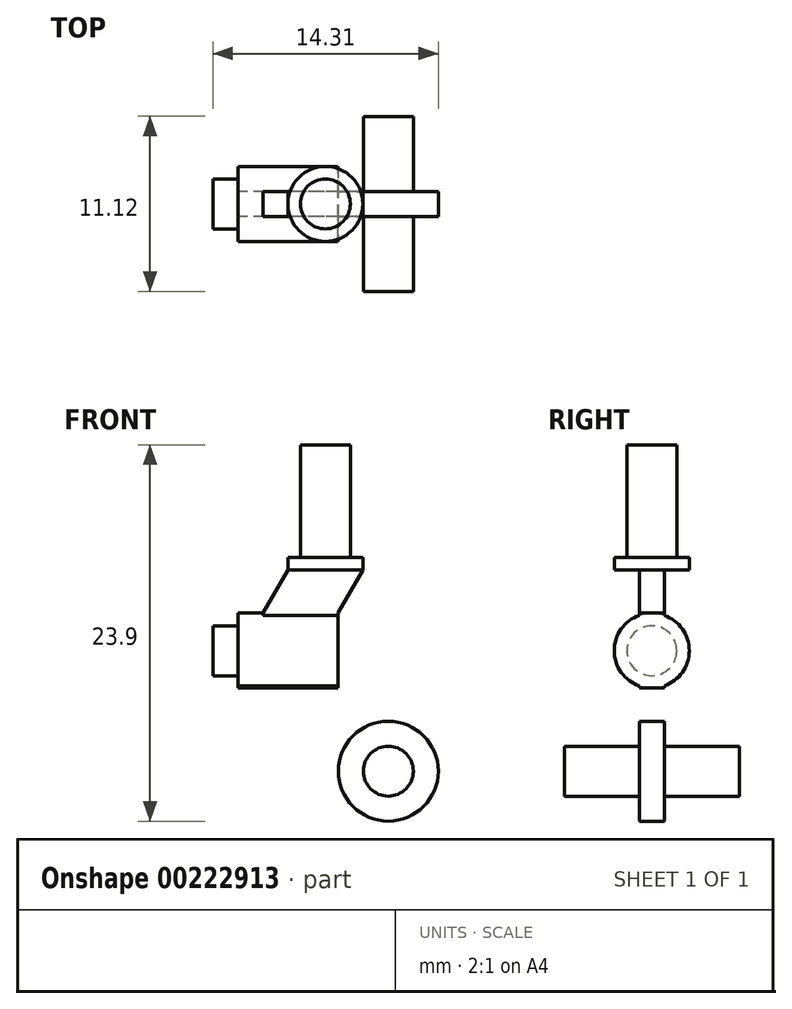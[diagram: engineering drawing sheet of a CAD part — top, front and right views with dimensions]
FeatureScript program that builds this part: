
annotation { "Feature Type Name" : "Feature", "Feature Type Description" : "" }
export const myFeature = defineFeature(function(context is Context, id is Id, definition is map)
    precondition{}
    {
        {
            var Q0;
            Q0=qCreatedBy(makeId("Top.planeOp"),FACE);
            var sketch = newSketch(context, id + "F0", { "sketchPlane" : qUnion([Q0])});
            skCircle(sketch, "E0", {"center": v(0, 0) * mm, "radius": 2.38 * mm});
            skCircle(sketch, "E1", {"center": v(0, 0) * mm, "radius": 1.59 * mm});
            skSolve(sketch);
        }
        {
            var Q0;
            Q0=makeQuery(id+"F0.imprint","IMPRINT",FACE,{"disambiguationData":[TD([[makeQuery(id+"F0.imprint","IMPRINT",EDGE,{"derivedFrom":sQuery(id+"F0.wireOp",EDGE,"E0")}),1.0]])]});
            extrude(context, id + "F1", {"entities" : qUnion([Q0]), "depth" : 0.8 * mm});
        }
        {
            var Q0;
            Q0=makeQuery(id+"F0.imprint","IMPRINT",FACE,{"disambiguationData":[TD([[makeQuery(id+"F0.imprint","IMPRINT",EDGE,{"derivedFrom":sQuery(id+"F0.wireOp",EDGE,"E1")}),1.0]])]});
            extrude(context, id + "F2", {"entities" : qUnion([Q0]), "operationType" : NewBodyOperationType.ADD, "depth" : 7.94 * mm});
        }
        {
            var Q0;
            Q0=qCreatedBy(makeId("Front.planeOp"),FACE);
            var sketch = newSketch(context, id + "F3", { "sketchPlane" : qUnion([Q0])});
            skLineSegment(sketch, "E2", {"start": v(0, 0) * mm, "end": v(-2.38, 0) * mm});
            skLineSegment(sketch, "E3", {"start": v(0, 0) * mm, "end": v(2.38, 0) * mm});
            skLineSegment(sketch, "E4", {"start": v(2.38, 0) * mm, "end": v(0.8, -2.75) * mm});
            skLineSegment(sketch, "E5", {"start": v(-2.38, 0) * mm, "end": v(-3.97, -2.75) * mm});
            skLineSegment(sketch, "E6", {"start": v(-3.97, -2.75) * mm, "end": v(0.8, -2.75) * mm});
            skLineSegment(sketch, "E7.bottom", {"start": v(0.8, -2.75) * mm, "end": v(-5.56, -2.75) * mm});
            skLineSegment(sketch, "E7.top", {"start": v(0.8, -7.51) * mm, "end": v(-5.56, -7.51) * mm});
            skLineSegment(sketch, "E7.left", {"start": v(0.8, -2.75) * mm, "end": v(0.8, -7.51) * mm});
            skLineSegment(sketch, "E8", {"start": v(-5.56, -5.13) * mm, "end": v(0.8, -5.13) * mm});
            skPoint(sketch, "E9", {"position": v(0.8, -3.54) * mm});
            skPoint(sketch, "E10.MirrorP", {"position": v(0.8, -6.72) * mm});
            skLineSegment(sketch, "E11.bottom", {"start": v(0.8, -6.72) * mm, "end": v(-7.14, -6.72) * mm});
            skLineSegment(sketch, "E11.left", {"start": v(0.8, -6.72) * mm, "end": v(0.8, -3.54) * mm});
            skLineSegment(sketch, "E11.right", {"start": v(-7.14, -6.72) * mm, "end": v(-7.14, -3.54) * mm});
            skLineSegment(sketch, "E12", {"start": v(-7.14, -5.13) * mm, "end": v(-5.56, -5.13) * mm});
            skLineSegment(sketch, "E13", {"start": v(-5.56, -2.75) * mm, "end": v(-5.56, -3.54) * mm});
            skLineSegment(sketch, "E14", {"start": v(-7.14, -3.54) * mm, "end": v(-5.56, -3.54) * mm});
            skLineSegment(sketch, "E15.MirrorCS", {"start": v(-7.14, -6.72) * mm, "end": v(-5.56, -6.72) * mm});
            skLineSegment(sketch, "E16.MirrorCS", {"start": v(-5.56, -7.51) * mm, "end": v(-5.56, -6.72) * mm});
            skLineSegment(sketch, "E17", {"start": v(0.8, -7.51) * mm, "end": v(3.04, -9.76) * mm});
            skLineSegment(sketch, "E18", {"start": v(-5.56, -7.51) * mm, "end": v(1.18, -14.25) * mm});
            skLineSegment(sketch, "E19", {"start": v(1.18, -14.25) * mm, "end": v(3.04, -9.76) * mm});
            skLineSegment(sketch, "E20.top", {"start": v(-3.97, -3.54) * mm, "end": v(0.8, -3.54) * mm});
            skLineSegment(sketch, "E20.left", {"start": v(-3.97, -2.75) * mm, "end": v(-3.97, -3.54) * mm});
            skLineSegment(sketch, "E20.right", {"start": v(0.8, -2.75) * mm, "end": v(0.8, -3.54) * mm});
            skCircle(sketch, "E21", {"center": v(4, -12.78) * mm, "radius": 3.18 * mm});
            skPoint(sketch, "E21.first.point", {"position": v(1.18, -14.25) * mm});
            skPoint(sketch, "E21.third.point", {"position": v(7.15, -13.17) * mm});
            skLineSegment(sketch, "E22", {"start": v(4, -12.78) * mm, "end": v(7.17, -12.78) * mm});
            skSolve(sketch);
        }
        {
            var Q0;
            Q0=makeQuery(id+"F3.imprint","IMPRINT",FACE,{"disambiguationData":[TD([[makeQuery(id+"F3.imprint","IMPRINT",EDGE,{"derivedFrom":sQuery(id+"F3.wireOp",EDGE,"E2")}),1.0]])]});
            var Q1;
            Q1=makeQuery(id+"F3.imprint","IMPRINT",FACE,{"disambiguationData":[TD([[makeQuery(id+"F3.imprint","IMPRINT",EDGE,{"derivedFrom":sQuery(id+"F3.wireOp",EDGE,"E6")}),-1.0]])]});
            var Q2;
            Q2=makeQuery(id+"F3.imprint","IMPRINT",FACE,{"disambiguationData":[TD([[makeQuery(id+"F3.imprint","IMPRINT",EDGE,{"derivedFrom":sQuery(id+"F3.wireOp",EDGE,"E7.left")}),-1.0]])]});
            var Q3;
            Q3=makeQuery(id+"F3.imprint","IMPRINT",FACE,{"disambiguationData":[TD([[makeQuery(id+"F3.imprint","IMPRINT",EDGE,{"derivedFrom":sQuery(id+"F3.wireOp",EDGE,"E7.top")}),1.0]])]});
            var Q4;
            {var subQ0=sQuery(id+"F3.wireOp",EDGE,"E19");Q4=makeQuery(id+"F3.imprint","IMPRINT",FACE,{"disambiguationData":[TD([[makeQuery(id+"F3.imprint","IMPRINT",EDGE,{"derivedFrom":subQ0}),1.0]])]});}
            var Q5;
            {var subQ0=sQuery(id+"F3.wireOp",EDGE,"E19");Q5=makeQuery(id+"F3.imprint","IMPRINT",FACE,{"disambiguationData":[TD([[makeQuery(id+"F3.imprint","IMPRINT",EDGE,{"derivedFrom":subQ0}),-1.0]])]});}
            extrude(context, id + "F4", {"entities" : qUnion([Q0, Q1, Q2, Q3, Q4, Q5]), "operationType" : NewBodyOperationType.ADD, "endBound" : BoundingType.SYMMETRIC, "depth" : 1.59 * mm});
        }
        {
            var Q0;
            Q0=makeQuery(id+"F3.imprint","IMPRINT",FACE,{"disambiguationData":[TD([[makeQuery(id+"F3.imprint","IMPRINT",EDGE,{"derivedFrom":sQuery(id+"F3.wireOp",EDGE,"E7.bottom")}),1.0]])]});
            var Q1;
            Q1=makeQuery(id+"F3.imprint","IMPRINT",FACE,{"disambiguationData":[TD([[makeQuery(id+"F3.imprint","IMPRINT",EDGE,{"derivedFrom":sQuery(id+"F3.wireOp",EDGE,"E6")}),-1.0]])]});
            var Q2;
            Q2=sQuery(id+"F3.wireOp",EDGE,"E8");
            revolve(context, id + "F5", {"operationType" : NewBodyOperationType.ADD, "entities" : qUnion([Q0, Q1]), "axis" : qUnion([Q2]), "revolveType" : RevolveType.FULL});
        }
        {
            var Q0;
            Q0=makeQuery(id+"F4.opExtrude","CAP_FACE",FACE,{"disambiguationData":[OSD([sQuery(id+"F3.wireOp",EDGE,"E7.left"),sQuery(id+"F3.wireOp",EDGE,"E11.bottom"),sQuery(id+"F3.wireOp",EDGE,"E16.MirrorCS"),sQuery(id+"F3.wireOp",EDGE,"E17"),sQuery(id+"F3.wireOp",EDGE,"E18"),sQuery(id+"F3.wireOp",EDGE,"E21")])],"isStart":false});
            var sketch = newSketch(context, id + "F6", { "sketchPlane" : qUnion([Q0])});
            skCircle(sketch, "E23", {"center": v(4, -12.78) * mm, "radius": 1.59 * mm});
            skSolve(sketch);
        }
        {
            var Q0;
            Q0 = qSketchRegion(id + "F6", true);
            extrude(context, id + "F7", {"entities" : qUnion([Q0]), "operationType" : NewBodyOperationType.ADD, "depth" : 4.76 * mm});
        }
        {
            var Q0;
            Q0=makeQuery(id+"F4.opExtrude","CAP_FACE",FACE,{"disambiguationData":[OSD([sQuery(id+"F3.wireOp",EDGE,"E7.left"),sQuery(id+"F3.wireOp",EDGE,"E11.bottom"),sQuery(id+"F3.wireOp",EDGE,"E16.MirrorCS"),sQuery(id+"F3.wireOp",EDGE,"E17"),sQuery(id+"F3.wireOp",EDGE,"E18"),sQuery(id+"F3.wireOp",EDGE,"E21")])],"isStart":true});
            var sketch = newSketch(context, id + "F8", { "sketchPlane" : qUnion([Q0])});
            skCircle(sketch, "E24", {"center": v(-4, -12.78) * mm, "radius": 1.59 * mm});
            skSolve(sketch);
        }
        {
            var Q0;
            Q0 = qSketchRegion(id + "F8", true);
            extrude(context, id + "F9", {"entities" : qUnion([Q0]), "operationType" : NewBodyOperationType.ADD, "depth" : 4.76 * mm});
        }
    });
